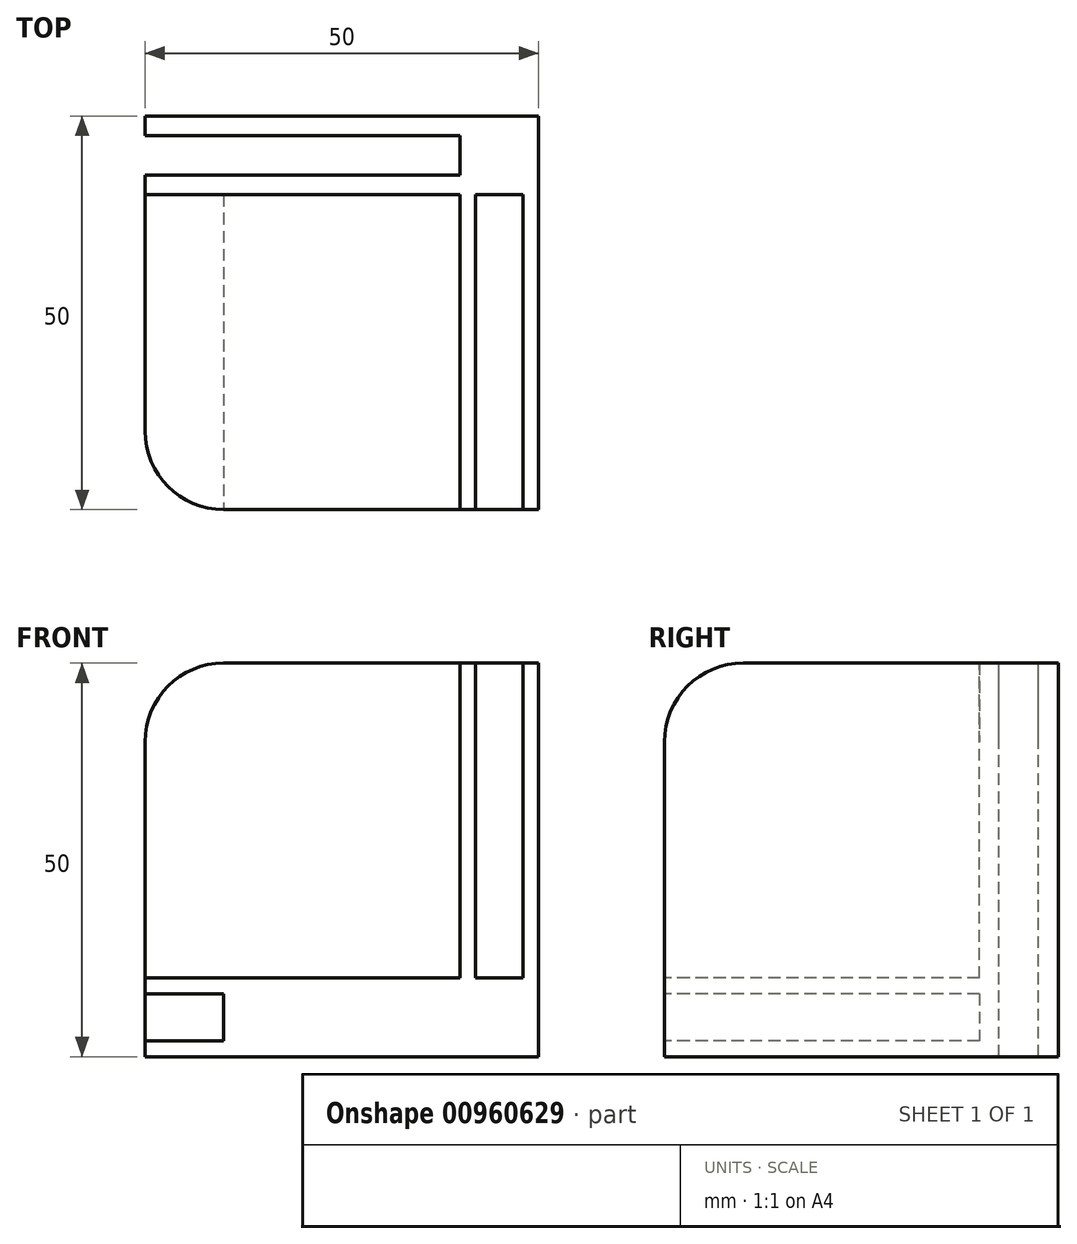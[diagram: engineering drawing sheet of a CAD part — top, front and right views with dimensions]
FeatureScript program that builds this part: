
annotation { "Feature Type Name" : "Feature", "Feature Type Description" : "" }
export const myFeature = defineFeature(function(context is Context, id is Id, definition is map)
    precondition{}
    {
        {
            var Q0;
            Q0=qCreatedBy(makeId("Top.planeOp"),FACE);
            var sketch = newSketch(context, id + "F0", { "sketchPlane" : qUnion([Q0])});
            skLineSegment(sketch, "E0.bottom", {"start": v(0, 0) * mm, "end": v(-50, 0) * mm});
            skLineSegment(sketch, "E0.top", {"start": v(0, -50) * mm, "end": v(-40, -50) * mm});
            skLineSegment(sketch, "E0.left", {"start": v(0, 0) * mm, "end": v(0, -50) * mm});
            skLineSegment(sketch, "E0.right", {"start": v(-50, 0) * mm, "end": v(-50, -40) * mm});
            skPoint(sketch, "E1.visualSharp", {"position": v(-50, -50) * mm});
            skArc(sketch, "E1.filletArc", {"start": v(-50, -40) * mm, "mid": v(-47.07, -47.07) * mm, "end": v(-40, -50) * mm});
            skSolve(sketch);
        }
        {
            var Q0;
            Q0=makeQuery(id+"F0.imprint","IMPRINT",FACE,{"disambiguationData":[TD([[makeQuery(id+"F0.imprint","IMPRINT",EDGE,{"derivedFrom":sQuery(id+"F0.wireOp",EDGE,"tNkWgY0K-5FoM-fzsk-HCrw-KOSka2LcS9h1.bottom")}),-1.0]])]});
            var Q1;
            Q1=makeQuery(id+"F0.imprint","IMPRINT",FACE,{"disambiguationData":[TD([[makeQuery(id+"F0.imprint","IMPRINT",EDGE,{"derivedFrom":sQuery(id+"F0.wireOp",EDGE,"E0.bottom")}),1.0]])]});
            var Q2;
            Q2=makeQuery(id+"F0.imprint","IMPRINT",FACE,{"disambiguationData":[TD([[makeQuery(id+"F0.imprint","IMPRINT",EDGE,{"derivedFrom":sQuery(id+"F0.wireOp",EDGE,"E0.top")}),-1.0]])]});
            var Q3;
            Q3=makeQuery(id+"F0.imprint","IMPRINT",FACE,{"disambiguationData":[TD([[makeQuery(id+"F0.imprint","IMPRINT",EDGE,{"derivedFrom":sQuery(id+"F0.wireOp",EDGE,"fvIwUqZD-S5C8-yHxi-N0ak-uGxWySerV2bo.bottom")}),1.0]])]});
            var Q4;
            Q4=makeQuery(id+"F0.imprint","IMPRINT",FACE,{"disambiguationData":[TD([[makeQuery(id+"F0.imprint","IMPRINT",EDGE,{"derivedFrom":sQuery(id+"F0.wireOp",EDGE,"JSCxDXyh-nDxv-V0qH-dKlW-7TGNpykFalIj.bottom")}),1.0]])]});
            extrude(context, id + "F1", {"entities" : qUnion([Q0, Q1, Q2, Q3, Q4]), "depth" : 10 * mm, "offsetDistance" : 25 * mm});
        }
        {
            var Q0;
            Q0=qCreatedBy(makeId("Right.planeOp"),FACE);
            var sketch = newSketch(context, id + "F2", { "sketchPlane" : qUnion([Q0])});
            skLineSegment(sketch, "E2.bottom", {"start": v(0, 10) * mm, "end": v(-50, 10) * mm});
            skLineSegment(sketch, "E2.top", {"start": v(0, 50) * mm, "end": v(-40, 50) * mm});
            skLineSegment(sketch, "E2.left", {"start": v(0, 10) * mm, "end": v(0, 50) * mm});
            skLineSegment(sketch, "E2.right", {"start": v(-50, 10) * mm, "end": v(-50, 40) * mm});
            skPoint(sketch, "E3.visualSharp", {"position": v(-50, 50) * mm});
            skArc(sketch, "E3.filletArc", {"start": v(-40, 50) * mm, "mid": v(-47.07, 47.07) * mm, "end": v(-50, 40) * mm});
            skSolve(sketch);
        }
        {
            var Q0;
            Q0=makeQuery(id+"F2.imprint","IMPRINT",FACE,{"disambiguationData":[TD([[makeQuery(id+"F2.imprint","IMPRINT",EDGE,{"derivedFrom":sQuery(id+"F2.wireOp",EDGE,"E2.bottom")}),-1.0]])]});
            extrude(context, id + "F3", {"entities" : qUnion([Q0]), "operationType" : NewBodyOperationType.ADD, "oppositeDirection" : true, "depth" : 10 * mm, "offsetDistance" : 25 * mm});
        }
        {
            var Q0;
            Q0=qCreatedBy(makeId("Front.planeOp"),FACE);
            var sketch = newSketch(context, id + "F4", { "sketchPlane" : qUnion([Q0])});
            skLineSegment(sketch, "E4.bottom", {"start": v(-10, 10) * mm, "end": v(-50, 10) * mm});
            skLineSegment(sketch, "E4.top", {"start": v(-10, 50) * mm, "end": v(-40, 50) * mm});
            skLineSegment(sketch, "E4.left", {"start": v(-10, 10) * mm, "end": v(-10, 50) * mm});
            skLineSegment(sketch, "E4.right", {"start": v(-50, 10) * mm, "end": v(-50, 40) * mm});
            skPoint(sketch, "E5.visualSharp", {"position": v(-50, 50) * mm});
            skArc(sketch, "E5.filletArc", {"start": v(-40, 50) * mm, "mid": v(-47.07, 47.07) * mm, "end": v(-50, 40) * mm});
            skSolve(sketch);
        }
        {
            var Q0;
            Q0=makeQuery(id+"F4.imprint","IMPRINT",FACE,{"disambiguationData":[TD([[makeQuery(id+"F4.imprint","IMPRINT",EDGE,{"derivedFrom":sQuery(id+"F4.wireOp",EDGE,"E4.bottom")}),-1.0]])]});
            extrude(context, id + "F5", {"entities" : qUnion([Q0]), "operationType" : NewBodyOperationType.ADD, "depth" : 10 * mm, "offsetDistance" : 25 * mm});
        }
        {
            var Q0;
            Q0=makeQuery(id+"F3.boolean.opBoolean","MERGE",FACE,{"derivedFrom":[makeQuery(id+"F1.opExtrude","SWEPT_FACE",FACE,{"disambiguationData":[OSD([sQuery(id+"F0.wireOp",EDGE,"E0.top")])]}),makeQuery(id+"F3.opExtrude","SWEPT_FACE",FACE,{"disambiguationData":[OSD([sQuery(id+"F2.wireOp",EDGE,"E2.right")])]})]});
            var sketch = newSketch(context, id + "F6", { "sketchPlane" : qUnion([Q0])});
            skLineSegment(sketch, "E6.bottom", {"start": v(-10, 2) * mm, "end": v(-60, 2) * mm});
            skLineSegment(sketch, "E6.top", {"start": v(-10, 8) * mm, "end": v(-60, 8) * mm});
            skLineSegment(sketch, "E6.left", {"start": v(-10, 2) * mm, "end": v(-10, 8) * mm});
            skLineSegment(sketch, "E6.right", {"start": v(-60, 2) * mm, "end": v(-60, 8) * mm});
            skLineSegment(sketch, "E7.bottom", {"start": v(-10, 2) * mm, "end": v(-15, 2) * mm});
            skLineSegment(sketch, "E7.top", {"start": v(-10, 52) * mm, "end": v(-15, 52) * mm});
            skLineSegment(sketch, "E8.bottom", {"start": v(-2, 10) * mm, "end": v(-8, 10) * mm});
            skLineSegment(sketch, "E8.top", {"start": v(-2, 60) * mm, "end": v(-8, 60) * mm});
            skLineSegment(sketch, "E8.left", {"start": v(-2, 10) * mm, "end": v(-2, 60) * mm});
            skLineSegment(sketch, "E8.right", {"start": v(-8, 10) * mm, "end": v(-8, 60) * mm});
            skSolve(sketch);
        }
        {
            var Q0;
            {var subQ5=sQuery(id+"F6.wireOp",EDGE,"E7.bottom");Q0=makeQuery(id+"F6.imprint","IMPRINT",FACE,{"disambiguationData":[TD([[makeQuery(id+"F6.imprint","IMPRINT",EDGE,{"derivedFrom":subQ5}),-1.0]])]});}
            var Q1;
            {var subQ0=sQuery(id+"F6.wireOp",EDGE,"E7.right");var subQ5=sQuery(id+"F6.wireOp",EDGE,"E6.top");var subQ7=makeQuery(id+"F6.imprint","INTERSECT",VERTEX,{"derivedFrom":[subQ5,subQ0]});Q1=makeQuery(id+"F6.imprint","IMPRINT",FACE,{"disambiguationData":[TD([[makeQuery(id+"F6.imprint","IMPRINT",EDGE,{"disambiguationData":[TD([[subQ7,-1.0]])],"derivedFrom":subQ5}),1.0]])]});}
            var Q2;
            {var subQ0=sQuery(id+"F6.wireOp",EDGE,"E6.right");Q2=makeQuery(id+"F6.imprint","IMPRINT",FACE,{"disambiguationData":[TD([[makeQuery(id+"F6.imprint","IMPRINT",EDGE,{"derivedFrom":subQ0}),-1.0]])]});}
            var Q3;
            {var subQ0=sQuery(id+"F6.wireOp",EDGE,"E8.bottom");Q3=makeQuery(id+"F6.imprint","IMPRINT",FACE,{"disambiguationData":[TD([[makeQuery(id+"F6.imprint","IMPRINT",EDGE,{"derivedFrom":subQ0}),-1.0]])]});}
            var Q4;
            {var subQ0=sQuery(id+"F6.wireOp",EDGE,"E8.top");Q4=makeQuery(id+"F6.imprint","IMPRINT",FACE,{"disambiguationData":[TD([[makeQuery(id+"F6.imprint","IMPRINT",EDGE,{"derivedFrom":subQ0}),1.0]])]});}
            extrude(context, id + "F7", {"entities" : qUnion([Q0, Q1, Q2, Q3, Q4]), "operationType" : NewBodyOperationType.REMOVE, "oppositeDirection" : true, "depth" : 40 * mm, "offsetDistance" : 25 * mm});
        }
        {
            var Q0;
            Q0=makeQuery(id+"F5.boolean.opBoolean","MERGE",FACE,{"derivedFrom":[makeQuery(id+"F3.opExtrude","SWEPT_FACE",FACE,{"disambiguationData":[OSD([sQuery(id+"F2.wireOp",EDGE,"E2.top")])]}),makeQuery(id+"F5.opExtrude","SWEPT_FACE",FACE,{"disambiguationData":[OSD([sQuery(id+"F4.wireOp",EDGE,"E4.top")])]})]});
            var sketch = newSketch(context, id + "F8", { "sketchPlane" : qUnion([Q0])});
            skLineSegment(sketch, "E9.bottom", {"start": v(-10, -2.5) * mm, "end": v(-60, -2.5) * mm});
            skLineSegment(sketch, "E9.top", {"start": v(-10, -7.5) * mm, "end": v(-60, -7.5) * mm});
            skLineSegment(sketch, "E9.left", {"start": v(-10, -2.5) * mm, "end": v(-10, -7.5) * mm});
            skLineSegment(sketch, "E9.right", {"start": v(-60, -2.5) * mm, "end": v(-60, -7.5) * mm});
            skSolve(sketch);
        }
        {
            var Q0;
            {var subQ0=sQuery(id+"F8.wireOp",EDGE,"E9.left");Q0=makeQuery(id+"F8.imprint","IMPRINT",FACE,{"disambiguationData":[TD([[makeQuery(id+"F8.imprint","IMPRINT",EDGE,{"derivedFrom":subQ0}),-1.0]])]});}
            var Q1;
            {var subQ0=sQuery(id+"F8.wireOp",EDGE,"E9.right");Q1=makeQuery(id+"F8.imprint","IMPRINT",FACE,{"disambiguationData":[TD([[makeQuery(id+"F8.imprint","IMPRINT",EDGE,{"derivedFrom":subQ0}),1.0]])]});}
            extrude(context, id + "F9", {"entities" : qUnion([Q0, Q1]), "operationType" : NewBodyOperationType.REMOVE, "endBound" : BoundingType.THROUGH_ALL, "oppositeDirection" : true, "depth" : 40 * mm, "offsetDistance" : 25 * mm});
        }
    });
